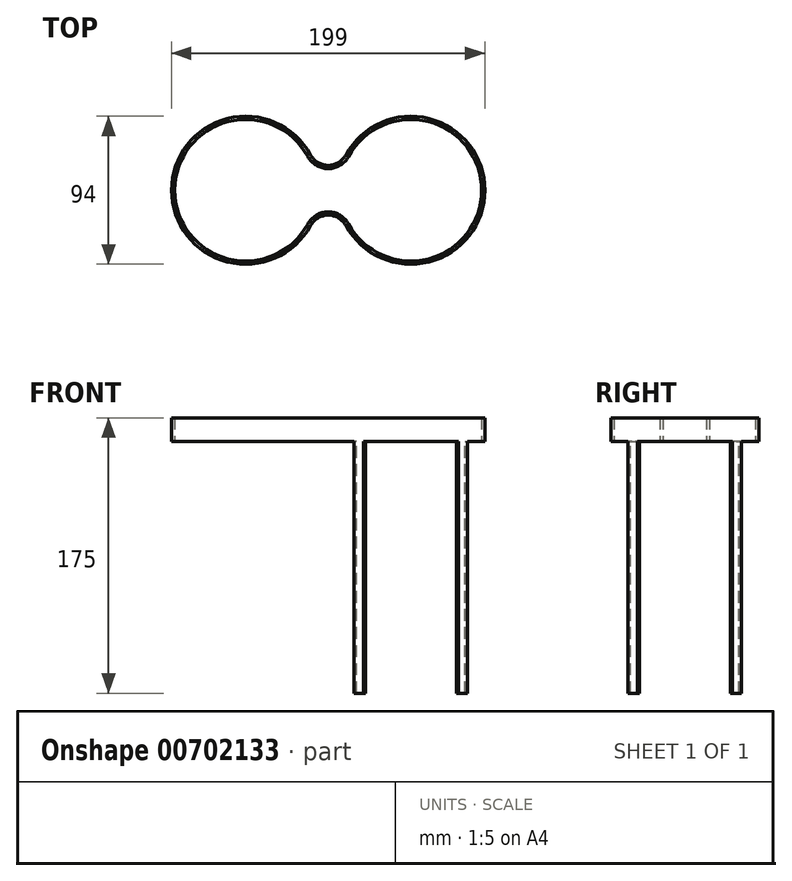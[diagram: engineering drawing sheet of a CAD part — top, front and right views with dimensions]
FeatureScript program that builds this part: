
annotation { "Feature Type Name" : "Feature", "Feature Type Description" : "" }
export const myFeature = defineFeature(function(context is Context, id is Id, definition is map)
    precondition{}
    {
        {
            var Q0;
            Q0=qCreatedBy(makeId("Top.planeOp"),FACE);
            var sketch = newSketch(context, id + "F0", { "sketchPlane" : qUnion([Q0])});
            skArc(sketch, "E0", {"start": v(39.57, 21.43) * mm, "mid": v(-45, 0) * mm, "end": v(39.57, -21.43) * mm});
            skArc(sketch, "E1", {"start": v(65.43, -21.43) * mm, "mid": v(150, 0) * mm, "end": v(65.43, 21.43) * mm});
            skArc(sketch, "E2", {"start": v(41.32, 22.4) * mm, "mid": v(-47, 0) * mm, "end": v(41.32, -22.4) * mm});
            skArc(sketch, "E3", {"start": v(60.98, -16.46) * mm, "mid": v(151.89, -3.26) * mm, "end": v(63.68, 22.4) * mm});
            skArc(sketch, "E4", {"start": v(63.73, -22.5) * mm, "mid": v(52.5, -15.78) * mm, "end": v(41.27, -22.5) * mm});
            skArc(sketch, "E5.MirrorCS", {"start": v(63.73, 22.5) * mm, "mid": v(52.5, 15.78) * mm, "end": v(41.27, 22.5) * mm});
            skArc(sketch, "E6.0", {"start": v(65.5, 21.55) * mm, "mid": v(52.5, 13.78) * mm, "end": v(39.5, 21.55) * mm});
            skArc(sketch, "E7.0", {"start": v(65.5, -21.55) * mm, "mid": v(52.5, -13.78) * mm, "end": v(39.5, -21.55) * mm});
            skSolve(sketch);
        }
        {
            var Q0;
            {var subQ4=sQuery(id+"F0.wireOp",EDGE,"E0");Q0=makeQuery(id+"F0.imprint","IMPRINT",FACE,{"disambiguationData":[TD([[makeQuery(id+"F0.imprint","IMPRINT",EDGE,{"derivedFrom":subQ4}),-1.0]])]});}
            extrude(context, id + "F1", {"entities" : qUnion([Q0]), "depth" : 15 * mm, "offsetDistance" : 25 * mm});
        }
        {
            var Q0;
            Q0=makeQuery(id+"F1.opExtrude","CAP_FACE",FACE,{"disambiguationData":[OSD([sQuery(id+"F0.wireOp",EDGE,"E0"),sQuery(id+"F0.wireOp",EDGE,"E1"),sQuery(id+"F0.wireOp",EDGE,"E2"),sQuery(id+"F0.wireOp",EDGE,"E3"),sQuery(id+"F0.wireOp",EDGE,"E5.MirrorCS"),sQuery(id+"F0.wireOp",EDGE,"E4"),sQuery(id+"F0.wireOp",EDGE,"E6.0"),sQuery(id+"F0.wireOp",EDGE,"E7.0")])],"isStart":true});
            var sketch = newSketch(context, id + "F2", { "sketchPlane" : qUnion([Q0])});
            skArc(sketch, "E8.0", {"start": v(69, 30.21) * mm, "mid": v(71.77, 33.23) * mm, "end": v(74.79, 36) * mm});
            skArc(sketch, "E9.0", {"start": v(70.53, 28.93) * mm, "mid": v(73.18, 31.82) * mm, "end": v(76.07, 34.47) * mm});
            skLineSegment(sketch, "E10", {"start": v(76.07, 34.47) * mm, "end": v(74.79, 36) * mm});
            skLineSegment(sketch, "E11.MirrorCS", {"start": v(70.53, 28.93) * mm, "end": v(69, 30.21) * mm});
            skPoint(sketch, "E12.orphan", {"position": v(65.5, -21.55) * mm});
            skPoint(sketch, "E13.orphan", {"position": v(63.73, -22.5) * mm});
            skPoint(sketch, "E14.orphan", {"position": v(65.5, 21.55) * mm});
            skPoint(sketch, "E15.orphan", {"position": v(63.73, 22.5) * mm});
            skLineSegment(sketch, "E16", {"start": v(71.77, 33.23) * mm, "end": v(105, 0) * mm});
            skArc(sketch, "E17.1.0", {"start": v(76.07, -34.47) * mm, "mid": v(73.18, -31.82) * mm, "end": v(70.53, -28.93) * mm});
            skLineSegment(sketch, "E17.1.1", {"start": v(70.53, -28.93) * mm, "end": v(69, -30.21) * mm});
            skArc(sketch, "E17.1.2", {"start": v(74.79, -36) * mm, "mid": v(71.77, -33.23) * mm, "end": v(69, -30.21) * mm});
            skLineSegment(sketch, "E17.1.3", {"start": v(76.07, -34.47) * mm, "end": v(74.79, -36) * mm});
            skArc(sketch, "E17.2.0", {"start": v(139.47, -28.93) * mm, "mid": v(136.82, -31.82) * mm, "end": v(133.93, -34.47) * mm});
            skLineSegment(sketch, "E17.2.1", {"start": v(133.93, -34.47) * mm, "end": v(135.21, -36) * mm});
            skArc(sketch, "E17.2.2", {"start": v(141, -30.21) * mm, "mid": v(138.23, -33.23) * mm, "end": v(135.21, -36) * mm});
            skLineSegment(sketch, "E17.2.3", {"start": v(139.47, -28.93) * mm, "end": v(141, -30.21) * mm});
            skArc(sketch, "E17.3.0", {"start": v(133.93, 34.47) * mm, "mid": v(136.82, 31.82) * mm, "end": v(139.47, 28.93) * mm});
            skLineSegment(sketch, "E17.3.1", {"start": v(139.47, 28.93) * mm, "end": v(141, 30.21) * mm});
            skArc(sketch, "E17.3.2", {"start": v(135.21, 36) * mm, "mid": v(138.23, 33.23) * mm, "end": v(141, 30.21) * mm});
            skLineSegment(sketch, "E17.3.3", {"start": v(133.93, 34.47) * mm, "end": v(135.21, 36) * mm});
            skSolve(sketch);
        }
        {
            var Q0;
            {var subQ0=sQuery(id+"F2.wireOp",EDGE,"E10");Q0=makeQuery(id+"F2.imprint","IMPRINT",FACE,{"disambiguationData":[TD([[makeQuery(id+"F2.imprint","IMPRINT",EDGE,{"derivedFrom":subQ0}),1.0]])]});}
            var Q1;
            {var subQ0=sQuery(id+"F2.wireOp",EDGE,"E11.MirrorCS");Q1=makeQuery(id+"F2.imprint","IMPRINT",FACE,{"disambiguationData":[TD([[makeQuery(id+"F2.imprint","IMPRINT",EDGE,{"derivedFrom":subQ0}),-1.0]])]});}
            var Q2;
            Q2=makeQuery(id+"F2.imprint","IMPRINT",FACE,{"disambiguationData":[TD([[makeQuery(id+"F2.imprint","IMPRINT",EDGE,{"derivedFrom":sQuery(id+"F2.wireOp",EDGE,"E17.3.0")}),1.0]])]});
            var Q3;
            Q3=makeQuery(id+"F2.imprint","IMPRINT",FACE,{"disambiguationData":[TD([[makeQuery(id+"F2.imprint","IMPRINT",EDGE,{"derivedFrom":sQuery(id+"F2.wireOp",EDGE,"E17.2.0")}),1.0]])]});
            var Q4;
            Q4=makeQuery(id+"F2.imprint","IMPRINT",FACE,{"disambiguationData":[TD([[makeQuery(id+"F2.imprint","IMPRINT",EDGE,{"derivedFrom":sQuery(id+"F2.wireOp",EDGE,"E17.1.0")}),1.0]])]});
            extrude(context, id + "F3", {"entities" : qUnion([Q0, Q1, Q2, Q3, Q4]), "operationType" : NewBodyOperationType.ADD, "depth" : 160 * mm, "offsetDistance" : 25 * mm});
        }
    });
